# Revit family: 506_93d66b9cf9164f9584ce2551329499
name_source: partatom
category: Electrical Equipment
revit_build: Autodesk Revit 2018 (Build: 20170223_1515(x64)
units: mm (PartAtom-declared; Revit-internal decimal feet)

## family parameters
Always vertical = Yes
Cut with Voids When Loaded = No
Part Type = Equipment Switch
Room Calculation Point = No
Round Connector Dimension = Use Diameter
Shared = No
Work Plane-Based = No

## types (1)
- VCIN1A250-S0 vertical
    CAT0 = 1 mm  [stored 0.00328084 ft]
    DP = 500 mm  [stored 1.64042 ft]
    Description = Air curtain INDESSE, length 2,75m, ambient
    H1 = 194 mm  [stored 0.636483 ft]
    H2 = 200 mm
    H3 = 40 mm  [stored 0.131234 ft]
    HP = 117 mm  [stored 0.383858 ft]
    HP__ve = -117 mm  [stored -0.383858 ft]
    L = 2750 mm  [stored 9.02231 ft]
    L2D = 0 mm  [stored 0 ft]
    L__ve = -2750 mm  [stored -9.02231 ft]
    MC Active Power = 1 W
    MC CosPhi = 0.95
    MC Number of Poles = 3
    MC Product Code = VCIN1A250-S0 vertical
    MC Voltage = 0 V
    Manufacturer = 2VV
    PD = 1100 mm  [stored 3.60892 ft]
    URL = www.2vv.cz
    W2 = 252 mm  [stored 0.826772 ft]
    W22 = 126 mm  [stored 0.413386 ft]
    W2D = 0 mm  [stored 0 ft]
    XP = 276 mm
    YP = 1313 mm  [stored 4.30774 ft]
    ZH = 1375 mm  [stored 4.51115 ft]
    ZP = 127 mm  [stored 0.416667 ft]
    ZPD = 550 mm  [stored 1.80446 ft]
    magiApparentLoad = 1 VA
    magiPartTypeId = 506
    magiProductFamilyId = 93d66b9cf9164f9584ce2551329499
    magiProductId = 12007491d6a74960ba728cd4bcf831

note: [stored X ft] marks values corroborated as IEEE doubles in the binary element streams (Revit-internal decimal feet)

## geometry (parser evidence)
native form markers: Blend x2, Sweep x3
no freeform markers — native parametric forms only
